FCSTD DOCUMENT  (FreeCAD 0.17R7723 (Git))
Label: kfmOTC
License: All rights reserved
LicenseURL: http://en.wikipedia.org/wiki/All_rights_reserved
objects: Sketcher::SketchObject×8
note: 8 computed .brp shape members not serialized (recipe doc carries the construction recipe); baked Part::Feature solids carry a one-line shape summary decoded from their .brp

FEATURE [Sketcher::SketchObject] Sketch  label="foam board"
  sketch-geometry (4):
    g0: LineSegment StartX=35.4421 StartY=15.6252 StartZ=0 EndX=35.4421 EndY=777.625 EndZ=0
    g1: LineSegment StartX=35.4421 StartY=777.625 StartZ=0 EndX=543.442 EndY=777.625 EndZ=0
    g2: LineSegment StartX=543.442 StartY=777.625 StartZ=0 EndX=543.442 EndY=15.6252 EndZ=0
    g3: LineSegment StartX=543.442 StartY=15.6252 StartZ=0 EndX=35.4421 EndY=15.6252 EndZ=0
  constraints (10):
    c: Coincident(g0,g1)
    c: Coincident(g1,g2)
    c: Vertical(g2)
    c: Coincident(g2,g3)
    c: Coincident(g3,g0)
    c: Parallel(g0,g2)
    c: Parallel(g1,g3)
    c: Perpendicular(g2,g1)
    c: Distance(g1) = 508
    c: Distance(g0) = 762
FEATURE [Sketcher::SketchObject] Sketch001  label="core"
  ExternalGeometry = -> [Sketch]
  sketch-geometry (19):
    g0: LineSegment StartX=464.941 StartY=15.6252 StartZ=0 EndX=314.941 EndY=15.6252 EndZ=0
    g1: LineSegment StartX=314.941 StartY=15.6252 StartZ=0 EndX=35.4421 EndY=505.625 EndZ=0
    g2: LineSegment StartX=35.4421 StartY=505.625 StartZ=0 EndX=35.4421 EndY=565.625 EndZ=0
    g3: LineSegment StartX=35.4421 StartY=565.625 StartZ=0 EndX=365.442 EndY=565.625 EndZ=0
    g4: LineSegment StartX=387.779 StartY=395.625 StartZ=0 EndX=464.941 EndY=15.6252 EndZ=0
    g5: LineSegment StartX=365.442 StartY=505.625 StartZ=0 EndX=365.442 EndY=565.625 EndZ=0
    g6: LineSegment StartX=365.442 StartY=505.625 StartZ=0 EndX=387.779 EndY=395.625 EndZ=0
    g7: LineSegment StartX=387.779 StartY=395.625 StartZ=0 EndX=367.779 EndY=395.625 EndZ=0
    g8: LineSegment StartX=424.941 StartY=15.6252 StartZ=0 EndX=367.779 EndY=395.625 EndZ=0
    g9: LineSegment StartX=464.941 StartY=15.6252 StartZ=0 EndX=389.941 EndY=15.6252 EndZ=0
    g10: LineSegment StartX=314.941 StartY=15.6252 StartZ=0 EndX=352.441 EndY=15.6252 EndZ=0
    g11: LineSegment StartX=352.441 StartY=15.6252 StartZ=0 EndX=389.941 EndY=15.6252 EndZ=0
    g12: LineSegment StartX=335.442 StartY=525.625 StartZ=0 EndX=335.442 EndY=565.625 EndZ=0
    g13: LineSegment StartX=335.442 StartY=565.625 StartZ=0 EndX=65.4421 EndY=565.625 EndZ=0
    g14: LineSegment StartX=71.1462 StartY=515.625 StartZ=0 EndX=65.4421 EndY=525.625 EndZ=0
    g15: LineSegment StartX=181.146 StartY=515.625 StartZ=0 EndX=186.85 EndY=525.625 EndZ=0
    g16: LineSegment StartX=181.146 StartY=515.625 StartZ=0 EndX=71.1462 EndY=515.625 EndZ=0
    g17: LineSegment StartX=65.4421 StartY=525.625 StartZ=0 EndX=65.4421 EndY=565.625 EndZ=0
    g18: LineSegment StartX=335.442 StartY=525.625 StartZ=0 EndX=186.85 EndY=525.625 EndZ=0
  constraints (60):
    c: Coincident(g1,g2)
    c: Vertical(g2)
    c: Coincident(g2,g3)
    c: Coincident(g5,g3)
    c: Parallel(g2,g5)
    c: Parallel(g3,g0)
    c: Distance(g2) = 60
    c: Distance(g5) = 60
    c: Parallel(g0,g-3)
    c: Coincident(g6,g5)
    c: DistanceY(g4,g3) = 170
    c: Coincident(g4,g6)
    c: Distance(g3,g-3) = 550
    c: Distance(g0,g0) = 150
    c: DistanceX(g-4,g1) = 0
    c: Distance(g3) = 330
    c: DistanceY(g-4,g0) = 0
    c: Coincident(g4,g7)
    c: Parallel(g7,g3)
    c: Coincident(g8,g7)
    c: Distance(g5,g0) = 500
    c: Parallel(g6,g4)
    c: Coincident(g11,g10)
    c: Coincident(g11,g9)
    c: Equal(g10,g11)
    c: Parallel(g11,g10)
    c: Coincident(g10,g0)
    c: Coincident(g9,g0)
    c: Distance(g9) = 75
    c: Parallel(g11,g9)
    c: Coincident(g0,g4)
    c: DistanceX(g-4) = 35.4421
    c: DistanceY(g-4) = 15.6252
    c: Coincident(g1,g0)
    c: DistanceY(g0,g8) = 0
    c: Distance(g7) = 20
    c: Distance(g8,g0) = 40
    c: Distance(g-4,g1) = 490
    c: Distance(g-4,g0) = 279.499
    c: Coincident(g12,g13)
    c: DistanceX(g2,g13) = 30
    c: Parallel(g14,g1)
    c: DistanceX(g12,g3) = 30
    c: Parallel(g13,g3)
    c: DistanceY(g5,g12) = 20
    c: DistanceY(g13,g2) = 0
    c: Coincident(g15,g16)
    c: Coincident(g16,g14)
    c: Coincident(g14,g17)
    c: Coincident(g17,g13)
    c: Coincident(g12,g18)
    c: Coincident(g18,g15)
    c: DistanceX(g13,g14) = 0
    c: Distance(g14,g15) = 110
    c: Parallel(g18,g3)
    c: DistanceY(g15,g14) = 0
    c: Parallel(g16,g3)
    c: DistanceX(g12,g12) = 0
    c: DistanceY(g5,g15) = 10
    c: Equal(g14,g15)
FEATURE [Sketcher::SketchObject] Sketch002  label="wing tips"
  ExternalGeometry = -> [Sketch]
  MapMode = 2
  Support = -> [Sketch001]
  sketch-geometry (10):
    g0: LineSegment StartX=35.4421 StartY=777.625 StartZ=0 EndX=175.442 EndY=777.625 EndZ=0
    g1: LineSegment StartX=175.442 StartY=777.625 StartZ=0 EndX=25.1923 EndY=832.625 EndZ=0
    g2: LineSegment StartX=25.1923 StartY=842.625 StartZ=0 EndX=175.442 EndY=897.625 EndZ=0
    g3: LineSegment StartX=175.442 StartY=897.625 StartZ=0 EndX=35.4421 EndY=897.625 EndZ=0
    g4: LineSegment StartX=35.4421 StartY=897.625 StartZ=0 EndX=274.992 EndY=832.625 EndZ=0
    g5: LineSegment StartX=274.992 StartY=832.625 StartZ=0 EndX=274.992 EndY=842.625 EndZ=0
    g6: LineSegment StartX=274.992 StartY=842.625 StartZ=0 EndX=35.4421 EndY=777.625 EndZ=0
    g7: ArcOfCircle CenterX=27.0226 CenterY=837.625 CenterZ=0 NormalX=0 NormalY=0 NormalZ=1 Radius=5.32447 StartAngle=1.9217 EndAngle=4.36148
    g8: LineSegment [constr] StartX=274.992 StartY=832.625 StartZ=0 EndX=175.442 EndY=897.625 EndZ=0
    g9: LineSegment [constr] StartX=274.992 StartY=842.625 StartZ=0 EndX=175.442 EndY=777.625 EndZ=0
  constraints (26):
    c: Coincident(g0,g1)
    c: Coincident(g2,g3)
    c: Coincident(g3,g4)
    c: Coincident(g4,g5)
    c: Coincident(g5,g6)
    c: Coincident(g6,g0)
    c: Perpendicular(g0,g5)
    c: Parallel(g0,g3)
    c: Distance(g5) = 10
    c: Distance(g0,g2) = 120
    c: Distance(g3) = 140
    c: Equal(g0,g3)
    c: Equal(g2,g1)
    c: Equal(g6,g4)
    c: Tangent(g1,g7) = 1.5708
    c: Tangent(g2,g7) = 1.5708
    c: Distance(g1,g2) = 10
    c: Distance(g2) = 160
    c: Distance(g4,g2) = 250
    c: Coincident(g8,g4)
    c: Coincident(g8,g2)
    c: Coincident(g9,g5)
    c: Coincident(g9,g0)
    c: Equal(g9,g8)
    c: Parallel(g0,g-3)
    c: Coincident(g0,g-3)
FEATURE [Sketcher::SketchObject] Sketch003  label="mid"
  ExternalGeometry = -> [Sketch001]
  MapMode = 2
  Support = -> [Sketch002]
  sketch-geometry (13):
    g0: LineSegment StartX=42.4421 StartY=505.625 StartZ=0 EndX=321.941 EndY=15.6252 EndZ=0
    g1: LineSegment StartX=321.941 StartY=15.6252 StartZ=0 EndX=389.941 EndY=15.6252 EndZ=0
    g2: LineSegment StartX=389.941 StartY=15.6252 StartZ=0 EndX=200.442 EndY=505.625 EndZ=0
    g3: LineSegment StartX=365.442 StartY=505.625 StartZ=0 EndX=365.442 EndY=565.625 EndZ=0
    g4: LineSegment StartX=365.442 StartY=565.625 StartZ=0 EndX=42.4421 EndY=565.625 EndZ=0
    g5: LineSegment StartX=365.442 StartY=505.625 StartZ=0 EndX=200.442 EndY=505.625 EndZ=0
    g6: LineSegment StartX=42.4421 StartY=505.625 StartZ=0 EndX=42.4421 EndY=565.625 EndZ=0
    g7: LineSegment StartX=65.4421 StartY=565.625 StartZ=0 EndX=65.4421 EndY=525.625 EndZ=0
    g8: LineSegment StartX=65.4421 StartY=525.625 StartZ=0 EndX=71.3944 EndY=515.19 EndZ=0
    g9: LineSegment StartX=71.3944 StartY=515.19 StartZ=0 EndX=181.394 EndY=515.19 EndZ=0
    g10: LineSegment StartX=181.394 StartY=515.19 StartZ=0 EndX=187.613 EndY=525.625 EndZ=0
    g11: LineSegment StartX=187.613 StartY=525.625 StartZ=0 EndX=335.442 EndY=525.625 EndZ=0
    g12: LineSegment StartX=335.442 StartY=525.625 StartZ=0 EndX=335.442 EndY=565.625 EndZ=0
FEATURE [Sketcher::SketchObject] Sketch004  label="leading edge"
  ExternalGeometry = -> [Sketch001,Sketch003]
  MapMode = 2
  Support = -> [Sketch003]
  sketch-geometry (11):
    g0: LineSegment StartX=117.942 StartY=505.625 StartZ=0 EndX=42.4421 EndY=505.625 EndZ=0
    g1: LineSegment StartX=42.4421 StartY=505.625 StartZ=0 EndX=23.4421 EndY=505.625 EndZ=0
    g2: LineSegment StartX=23.4421 StartY=505.625 StartZ=0 EndX=13.7707 EndY=489.271 EndZ=0
    g3: LineSegment StartX=13.7707 StartY=489.271 StartZ=0 EndX=-24.6604 EndY=424.284 EndZ=0
    g4: LineSegment StartX=-24.6604 StartY=424.284 StartZ=0 EndX=277.744 EndY=-26.9822 EndZ=0
    g5: LineSegment StartX=277.744 StartY=-26.9822 StartZ=0 EndX=293.269 EndY=-0.729163 EndZ=0
    g6: LineSegment StartX=293.269 StartY=-0.729163 StartZ=0 EndX=302.941 EndY=15.6252 EndZ=0
    g7: LineSegment StartX=302.941 StartY=15.6252 StartZ=0 EndX=321.941 EndY=15.6252 EndZ=0
    g8: LineSegment StartX=321.941 StartY=15.6252 StartZ=0 EndX=352.441 EndY=15.6252 EndZ=0
    g9: LineSegment StartX=352.441 StartY=15.6252 StartZ=0 EndX=117.942 EndY=505.625 EndZ=0
    g10: LineSegment [constr] StartX=23.4421 StartY=505.625 StartZ=0 EndX=302.941 EndY=15.6252 EndZ=0
  constraints (29):
    c: Coincident(g0,g1)
    c: Coincident(g1,g2)
    c: Coincident(g2,g3)
    c: Coincident(g3,g4)
    c: Coincident(g4,g5)
    c: Coincident(g5,g6)
    c: Coincident(g6,g7)
    c: Coincident(g7,g8)
    c: Coincident(g8,g9)
    c: Coincident(g9,g0)
    c: Coincident(g8,g-3)
    c: Coincident(g-4,g7)
    c: Distance(g7) = 19
    c: Equal(g5,g8)
    c: Equal(g6,g7)
    c: Parallel(g5,g6)
    c: Parallel(g8,g7)
    c: DistanceY(g0,g-5) = 0
    c: Parallel(g1,g0)
    c: Parallel(g2,g3)
    c: DistanceX(g-6,g0) = 0
    c: Equal(g1,g2)
    c: Coincident(g10,g1)
    c: Coincident(g10,g6)
    c: DistanceY(g0,g0) = 0
    c: Symmetric(g4,g8,g10)
    c: Symmetric(g3,g0,g10)
    c: Equal(g1,g7)
    c: Distance(g0,g-5) = 82.5
FEATURE [Sketcher::SketchObject] Sketch005  label="center"
  ExternalGeometry = -> [Sketch003,Sketch001]
  MapMode = 2
  Support = -> [Sketch001]
  sketch-geometry (23):
    g0: LineSegment StartX=365.442 StartY=625.625 StartZ=0 EndX=42.4421 EndY=625.625 EndZ=0
    g1: LineSegment StartX=42.4421 StartY=625.625 StartZ=0 EndX=4.44212 EndY=625.625 EndZ=0
    g2: LineSegment StartX=4.44212 StartY=625.625 StartZ=0 EndX=-266.776 EndY=625.625 EndZ=0
    g3: LineSegment StartX=-266.776 StartY=625.625 StartZ=0 EndX=-266.776 EndY=505.625 EndZ=0
    g4: LineSegment StartX=-266.776 StartY=505.625 StartZ=0 EndX=4.44212 EndY=505.625 EndZ=0
    g5: LineSegment StartX=4.44212 StartY=505.625 StartZ=0 EndX=42.4421 EndY=505.625 EndZ=0
    g6: LineSegment StartX=42.4421 StartY=505.625 StartZ=0 EndX=365.442 EndY=505.625 EndZ=0
    g7: LineSegment StartX=42.4421 StartY=625.625 StartZ=0 EndX=42.4421 EndY=505.625 EndZ=0
    g8: LineSegment StartX=4.44212 StartY=625.625 StartZ=0 EndX=4.44212 EndY=505.625 EndZ=0
    g9: LineSegment [constr] StartX=335.442 StartY=565.625 StartZ=0 EndX=65.4421 EndY=565.625 EndZ=0
    g10: LineSegment StartX=65.4421 StartY=565.625 StartZ=0 EndX=65.4421 EndY=605.625 EndZ=0
    g11: LineSegment StartX=71.1462 StartY=615.625 StartZ=0 EndX=65.4421 EndY=605.625 EndZ=0
    g12: LineSegment StartX=71.1462 StartY=615.625 StartZ=0 EndX=181.146 EndY=615.625 EndZ=0
    g13: LineSegment StartX=181.146 StartY=615.625 StartZ=0 EndX=186.85 EndY=605.625 EndZ=0
    g14: LineSegment StartX=186.85 StartY=605.625 StartZ=0 EndX=335.442 EndY=605.625 EndZ=0
    g15: LineSegment StartX=335.442 StartY=605.625 StartZ=0 EndX=335.442 EndY=565.625 EndZ=0
    g16: LineSegment StartX=65.4421 StartY=565.625 StartZ=0 EndX=65.4421 EndY=525.625 EndZ=0
    g17: LineSegment StartX=65.4421 StartY=525.625 StartZ=0 EndX=71.1462 EndY=515.625 EndZ=0
    g18: LineSegment StartX=71.1462 StartY=515.625 StartZ=0 EndX=181.146 EndY=515.625 EndZ=0
    g19: LineSegment StartX=181.146 StartY=515.625 StartZ=0 EndX=186.85 EndY=525.625 EndZ=0
    g20: LineSegment StartX=186.85 StartY=525.625 StartZ=0 EndX=335.442 EndY=525.625 EndZ=0
    g21: LineSegment StartX=335.442 StartY=525.625 StartZ=0 EndX=335.442 EndY=565.625 EndZ=0
    g22: LineSegment StartX=365.442 StartY=505.625 StartZ=0 EndX=365.442 EndY=625.625 EndZ=0
  constraints (52):
    c: Coincident(g0,g1)
    c: Coincident(g1,g2)
    c: Coincident(g2,g3)
    c: Coincident(g3,g4)
    c: Coincident(g4,g5)
    c: Coincident(g5,g6)
    c: Parallel(g4,g5)
    c: Parallel(g5,g1)
    c: Parallel(g1,g0)
    c: Distance(g3) = 120
    c: Coincident(g5,g-3)
    c: Equal(g1,g5)
    c: Distance(g1) = 38
    c: Parallel(g0,g6)
    c: Equal(g6,g0)
    c: Equal(g2,g4)
    c: Coincident(g7,g0)
    c: Coincident(g7,g5)
    c: Coincident(g8,g1)
    c: Coincident(g8,g4)
    c: Coincident(g9,g-9)
    c: Coincident(g9,g-10)
    c: Coincident(g11,g10)
    c: Coincident(g11,g12)
    c: Coincident(g12,g13)
    c: Coincident(g13,g14)
    c: Coincident(g14,g15)
    c: Coincident(g15,g9)
    c: Coincident(g10,g9)
    c: Symmetric(g-8,g10,g9)
    c: Symmetric(g11,g-7,g9)
    c: Symmetric(g12,g-6,g9)
    c: Symmetric(g13,g-5,g9)
    c: Symmetric(g14,g-4,g9)
    c: Coincident(g9,g16)
    c: Coincident(g16,g-8)
    c: Coincident(g16,g17)
    c: Coincident(g17,g-7)
    c: Coincident(g17,g18)
    c: Coincident(g18,g-6)
    c: Coincident(g18,g19)
    c: Coincident(g19,g-5)
    c: Coincident(g19,g20)
    c: Coincident(g20,g-4)
    c: Coincident(g20,g21)
    c: Coincident(g21,g9)
    c: Distance(g6,g3) = 632.218
    c: Coincident(g22,g0)
    c: Coincident(g22,g6)
    c: Parallel(g20,g6)
    c: Perpendicular(g22,g0)
    c: DistanceX(g6,g-11) = 0
FEATURE [Sketcher::SketchObject] Sketch006  label="avionics lid"
  ExternalGeometry = -> [Sketch001,Sketch005]
  MapMode = 2
  Support = -> [Sketch005]
  sketch-geometry (4):
    g0: LineSegment StartX=51.4421 StartY=625.625 StartZ=0 EndX=51.4421 EndY=505.625 EndZ=0
    g1: LineSegment StartX=51.4421 StartY=505.625 StartZ=0 EndX=365.442 EndY=505.625 EndZ=0
    g2: LineSegment StartX=365.442 StartY=505.625 StartZ=0 EndX=365.442 EndY=625.625 EndZ=0
    g3: LineSegment StartX=365.442 StartY=625.625 StartZ=0 EndX=51.4421 EndY=625.625 EndZ=0
  constraints (10):
    c: Coincident(g3,g2)
    c: Coincident(g2,g-4)
    c: Coincident(g2,g1)
    c: Coincident(g-3,g1)
    c: Coincident(g3,g0)
    c: DistanceX(g-6,g0) = 9
    c: Coincident(g1,g0)
    c: DistanceY(g0,g-5) = 0
    c: DistanceY(g-6,g0) = 0
    c: Vertical(g0)
FEATURE [Sketcher::SketchObject] Sketch007  label="avionics spacer"
  ExternalGeometry = -> [Sketch005,Sketch001,Sketch003]
  MapMode = 2
  Support = -> [Sketch001]
  sketch-geometry (14):
    g0: LineSegment StartX=71.1462 StartY=615.625 StartZ=0 EndX=181.146 EndY=615.625 EndZ=0
    g1: LineSegment StartX=181.146 StartY=615.625 StartZ=0 EndX=186.85 EndY=605.625 EndZ=0
    g2: LineSegment StartX=186.85 StartY=605.625 StartZ=0 EndX=335.442 EndY=605.625 EndZ=0
    g3: LineSegment StartX=335.442 StartY=605.625 StartZ=0 EndX=335.442 EndY=525.625 EndZ=0
    g4: LineSegment StartX=335.442 StartY=525.625 StartZ=0 EndX=186.85 EndY=525.625 EndZ=0
    g5: LineSegment StartX=186.85 StartY=525.625 StartZ=0 EndX=181.394 EndY=515.19 EndZ=0
    g6: LineSegment StartX=181.394 StartY=515.19 StartZ=0 EndX=71.1462 EndY=515.625 EndZ=0
    g7: LineSegment StartX=71.1462 StartY=515.625 StartZ=0 EndX=65.4421 EndY=525.625 EndZ=0
    g8: LineSegment StartX=65.4421 StartY=525.625 StartZ=0 EndX=65.4421 EndY=605.625 EndZ=0
    g9: LineSegment StartX=65.4421 StartY=605.625 StartZ=0 EndX=71.1462 EndY=615.625 EndZ=0
    g10: LineSegment StartX=42.4421 StartY=625.625 StartZ=0 EndX=42.4421 EndY=505.625 EndZ=0
    g11: LineSegment StartX=42.4421 StartY=505.625 StartZ=0 EndX=365.442 EndY=505.625 EndZ=0
    g12: LineSegment StartX=365.442 StartY=505.625 StartZ=0 EndX=365.442 EndY=625.625 EndZ=0
    g13: LineSegment StartX=365.442 StartY=625.625 StartZ=0 EndX=42.4421 EndY=625.625 EndZ=0
  constraints (28):
    c: Coincident(g0,g1)
    c: Coincident(g1,g2)
    c: Coincident(g2,g3)
    c: Coincident(g3,g4)
    c: Coincident(g4,g5)
    c: Coincident(g5,g6)
    c: Coincident(g6,g7)
    c: Coincident(g7,g8)
    c: Coincident(g8,g9)
    c: Coincident(g9,g0)
    c: Coincident(g0,g-7)
    c: Coincident(g8,g-6)
    c: Coincident(g7,g-14)
    c: Coincident(g6,g-13)
    c: Coincident(g0,g-8)
    c: Coincident(g1,g-9)
    c: Coincident(g4,g-12)
    c: Coincident(g5,g-15)
    c: Coincident(g2,g-10)
    c: Coincident(g3,g-11)
    c: Coincident(g10,g-3)
    c: Coincident(g10,g-16)
    c: Coincident(g10,g11)
    c: Coincident(g11,g-17)
    c: Coincident(g11,g12)
    c: Coincident(g12,g-4)
    c: Coincident(g12,g13)
    c: Coincident(g13,g10)
